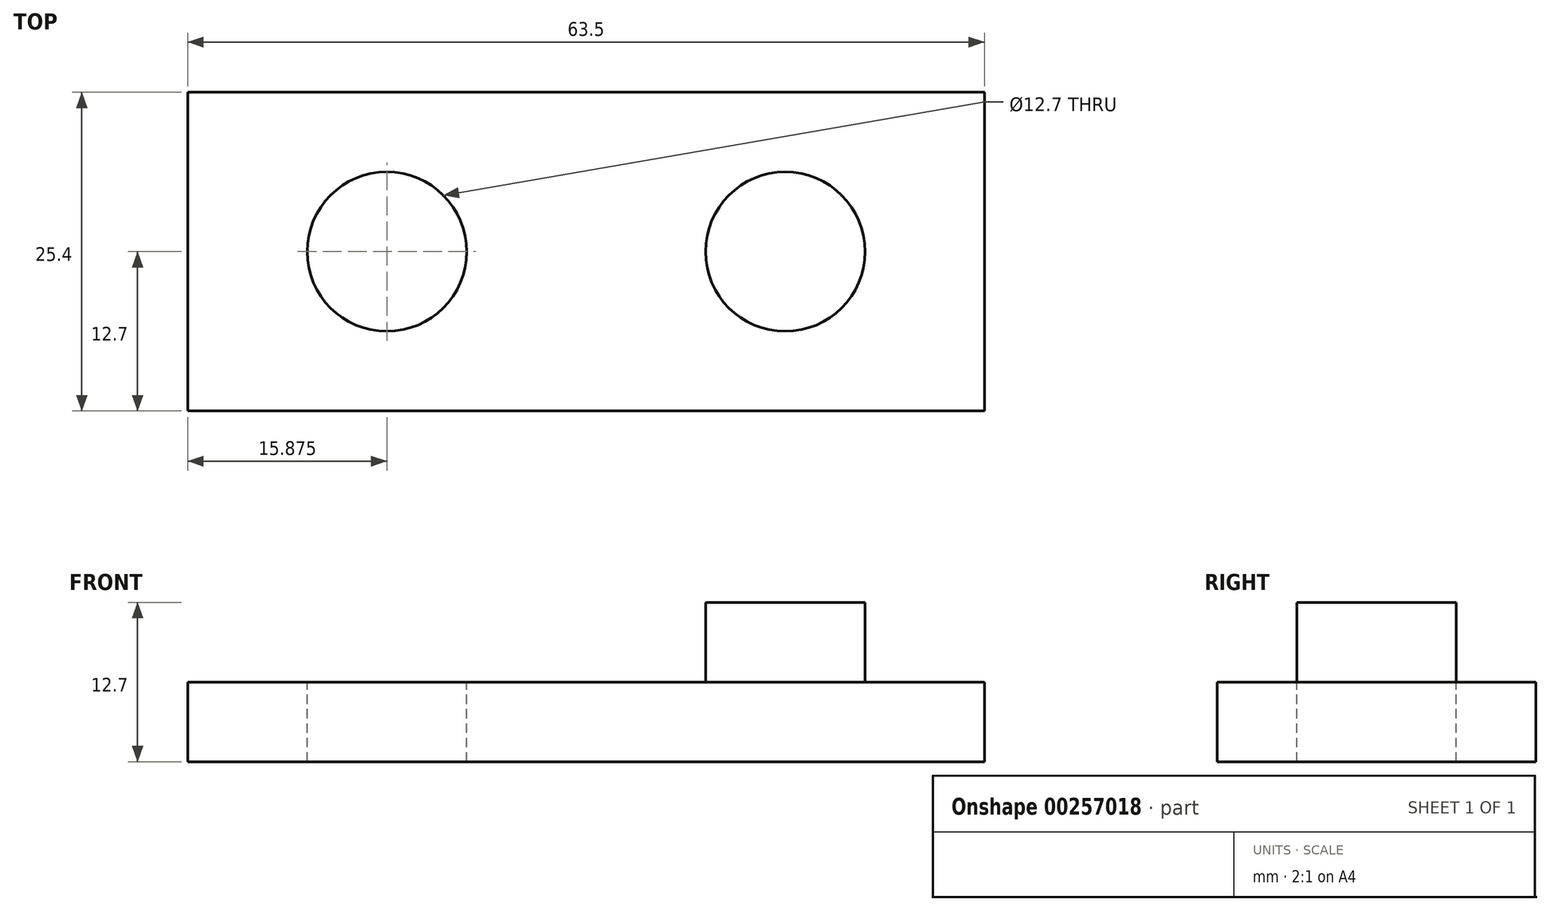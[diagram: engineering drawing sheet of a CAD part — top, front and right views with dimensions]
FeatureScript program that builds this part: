
annotation { "Feature Type Name" : "Feature", "Feature Type Description" : "" }
export const myFeature = defineFeature(function(context is Context, id is Id, definition is map)
    precondition{}
    {
        {
            var Q0;
            Q0=qCreatedBy(makeId("Top.planeOp"),FACE);
            var sketch = newSketch(context, id + "F0", { "sketchPlane" : qUnion([Q0])});
            skLineSegment(sketch, "E0.bottom", {"start": v(31.75, 12.7) * mm, "end": v(-31.75, 12.7) * mm});
            skLineSegment(sketch, "E0.top", {"start": v(31.75, -12.7) * mm, "end": v(-31.75, -12.7) * mm});
            skLineSegment(sketch, "E0.left", {"start": v(31.75, 12.7) * mm, "end": v(31.75, -12.7) * mm});
            skLineSegment(sketch, "E0.right", {"start": v(-31.75, 12.7) * mm, "end": v(-31.75, -12.7) * mm});
            skPoint(sketch, "E0.middle", {"position": v(0, 0) * mm});
            skSolve(sketch);
        }
        {
            var Q0;
            Q0 = qSketchRegion(id + "F0", true);
            extrude(context, id + "F1", {"entities" : qUnion([Q0]), "depth" : 6.35 * mm});
        }
        {
            var Q0;
            Q0=makeQuery(id+"F1.opExtrude","CAP_FACE",FACE,{"disambiguationData":[OSD([sQuery(id+"F0.wireOp",EDGE,"E0.bottom"),sQuery(id+"F0.wireOp",EDGE,"E0.top"),sQuery(id+"F0.wireOp",EDGE,"E0.left"),sQuery(id+"F0.wireOp",EDGE,"E0.right")])],"isStart":false});
            var sketch = newSketch(context, id + "F2", { "sketchPlane" : qUnion([Q0])});
            skCircle(sketch, "E1", {"center": v(-15.88, 0) * mm, "radius": 6.35 * mm});
            skLineSegment(sketch, "E2", {"start": v(-31.75, 0) * mm, "end": v(-15.88, 0) * mm, "construction": true});
            skLineSegment(sketch, "E3", {"start": v(0, 0) * mm, "end": v(-15.88, 0) * mm, "construction": true});
            skSolve(sketch);
        }
        {
            var Q0;
            Q0 = qSketchRegion(id + "F2", true);
            extrude(context, id + "F3", {"entities" : qUnion([Q0]), "operationType" : NewBodyOperationType.REMOVE, "endBound" : BoundingType.THROUGH_ALL, "oppositeDirection" : true, "depth" : 25.4 * mm});
        }
        {
            var Q0;
            Q0=makeQuery(id+"F1.opExtrude","CAP_FACE",FACE,{"disambiguationData":[OSD([sQuery(id+"F0.wireOp",EDGE,"E0.bottom"),sQuery(id+"F0.wireOp",EDGE,"E0.top"),sQuery(id+"F0.wireOp",EDGE,"E0.left"),sQuery(id+"F0.wireOp",EDGE,"E0.right")])],"isStart":false});
            var sketch = newSketch(context, id + "F4", { "sketchPlane" : qUnion([Q0])});
            skCircle(sketch, "E4", {"center": v(15.88, 0) * mm, "radius": 6.35 * mm});
            skLineSegment(sketch, "E5", {"start": v(0, 0) * mm, "end": v(15.88, 0) * mm, "construction": true});
            skLineSegment(sketch, "E6", {"start": v(31.75, 0) * mm, "end": v(15.88, 0) * mm, "construction": true});
            skSolve(sketch);
        }
        {
            var Q0;
            Q0 = qSketchRegion(id + "F4", true);
            extrude(context, id + "F5", {"entities" : qUnion([Q0]), "operationType" : NewBodyOperationType.ADD, "depth" : 6.35 * mm});
        }
    });
